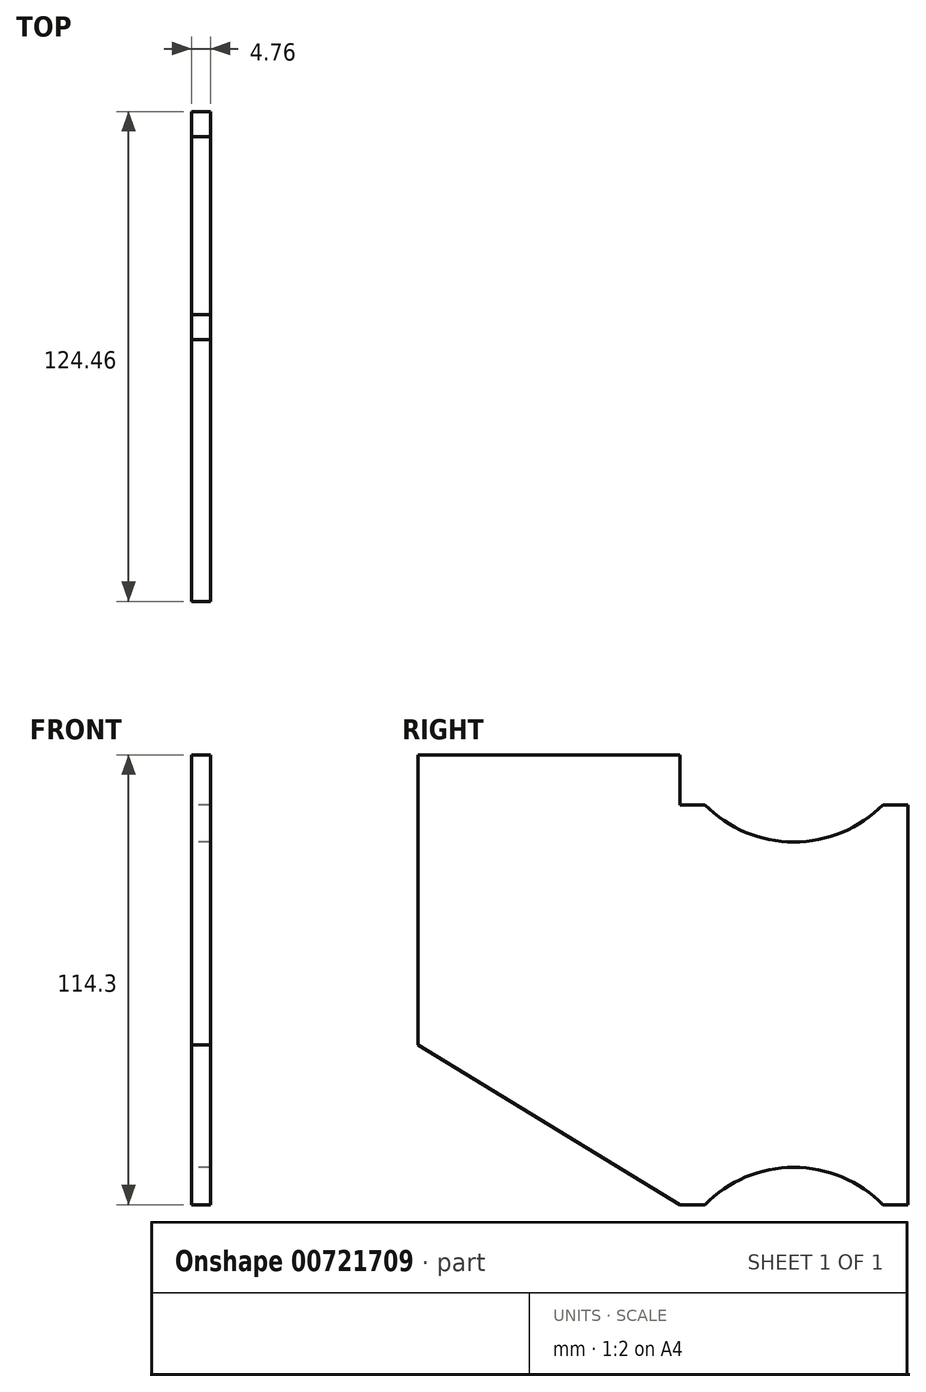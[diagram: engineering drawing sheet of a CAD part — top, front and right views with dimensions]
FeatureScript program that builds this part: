
annotation { "Feature Type Name" : "Feature", "Feature Type Description" : "" }
export const myFeature = defineFeature(function(context is Context, id is Id, definition is map)
    precondition{}
    {
        {
            var Q0;
            Q0=qCreatedBy(makeId("Right.planeOp"),FACE);
            var sketch = newSketch(context, id + "F0", { "sketchPlane" : qUnion([Q0])});
            skLineSegment(sketch, "E0.MirrorCS", {"start": v(139.7, -1252.54) * mm, "end": v(75.65, -1252.54) * mm, "construction": true});
            skLineSegment(sketch, "E1", {"start": v(204.78, -63.5) * mm, "end": v(124.46, -63.5) * mm, "construction": true});
            skLineSegment(sketch, "E2", {"start": v(124.46, -114.3) * mm, "end": v(118.11, -114.3) * mm});
            skLineSegment(sketch, "E3", {"start": v(66.55, -114.3) * mm, "end": v(0, -73.66) * mm});
            skLineSegment(sketch, "E4.MirrorCS", {"start": v(124.46, -12.7) * mm, "end": v(118.11, -12.7) * mm});
            skLineSegment(sketch, "E5", {"start": v(0, 0) * mm, "end": v(0, -73.66) * mm});
            skArc(sketch, "E6", {"start": v(72.9, -12.7) * mm, "mid": v(95.5, -22.16) * mm, "end": v(118.11, -12.7) * mm});
            skLineSegment(sketch, "E7.trimOffspring", {"start": v(72.9, -12.7) * mm, "end": v(66.55, -12.7) * mm});
            skLineSegment(sketch, "E8.MirrorCS", {"start": v(268.83, -1267.35) * mm, "end": v(204.78, -1267.35) * mm, "construction": true});
            skArc(sketch, "E9.MirrorCS", {"start": v(72.9, -114.3) * mm, "mid": v(95.5, -104.84) * mm, "end": v(118.11, -114.3) * mm});
            skLineSegment(sketch, "E10.trimOffspring", {"start": v(72.9, -114.3) * mm, "end": v(66.55, -114.3) * mm});
            skLineSegment(sketch, "E11", {"start": v(124.46, -12.7) * mm, "end": v(124.46, -114.3) * mm});
            skLineSegment(sketch, "E12", {"start": v(66.55, -12.7) * mm, "end": v(66.55, 0) * mm});
            skLineSegment(sketch, "E13", {"start": v(66.55, 0) * mm, "end": v(0, 0) * mm});
            skSolve(sketch);
        }
        {
            var Q0;
            Q0=qSketchRegion(id+"F0",true);
            extrude(context, id + "F1", {"entities" : qUnion([Q0]), "depth" : 4.76 * mm, "offsetDistance" : 25.4 * mm});
        }
    });
